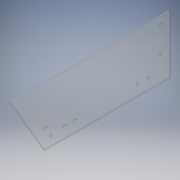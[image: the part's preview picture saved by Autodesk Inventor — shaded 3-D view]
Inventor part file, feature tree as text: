
AUTODESK INVENTOR PART (.ipt)
format: ipt  version: 2019 (Build 230136000, 136)  size: 130,560 bytes
history: native  units: in
note: dims shown in document units (in); Inventor stores cm internally (conversion verified against a paired STEP export)
features: sketch x3, hole x2, extrude x1
ambient origin geometry x8: Origin, YZ Plane, XZ Plane, XY Plane, X Axis, Y Axis, Z Axis, Center Point
bodies: Solid1 (feature_tree)
feature tree (6):
  extrude  "Extrusion1"  TaperAngle=150.0deg  [1 undecoded]
  hole  "Hole1"  [1 undecoded]
  hole  "Hole2"  [1 undecoded]
  sketch  "Sketch1"  dims[d0=3.5in d2=150.0deg]
  sketch  "Sketch2"  dims[d3=0.073in d4=0.0in d5=7.5in]
  sketch  "Sketch3"  dims[d6=0.6299in d8=0.6299in d9=0.63in d10=0.63in d11=0.63in d12=0.63in d13=6.283in d14=1.9in d15=0.15in d16=0.75in d17=0.375in d18=0.25in d19=0.5635in d20=0.432in d21=0.8108in d22=0.63in d23=0.63in d24=7.409in d25=7.09in d26=0.522in d27=0.522in d28=3.0in d29=1.5in d30=0.15in d31=0.75in d32=0.375in d33=0.25in d34=0.5635in d35=0.432in d36=0.8108in]
note: 3 required parameter values undecoded (feature->parameter linkage not recoverable at this tier; creation-order binding heuristic only, values carry confidence <= 0.55)
